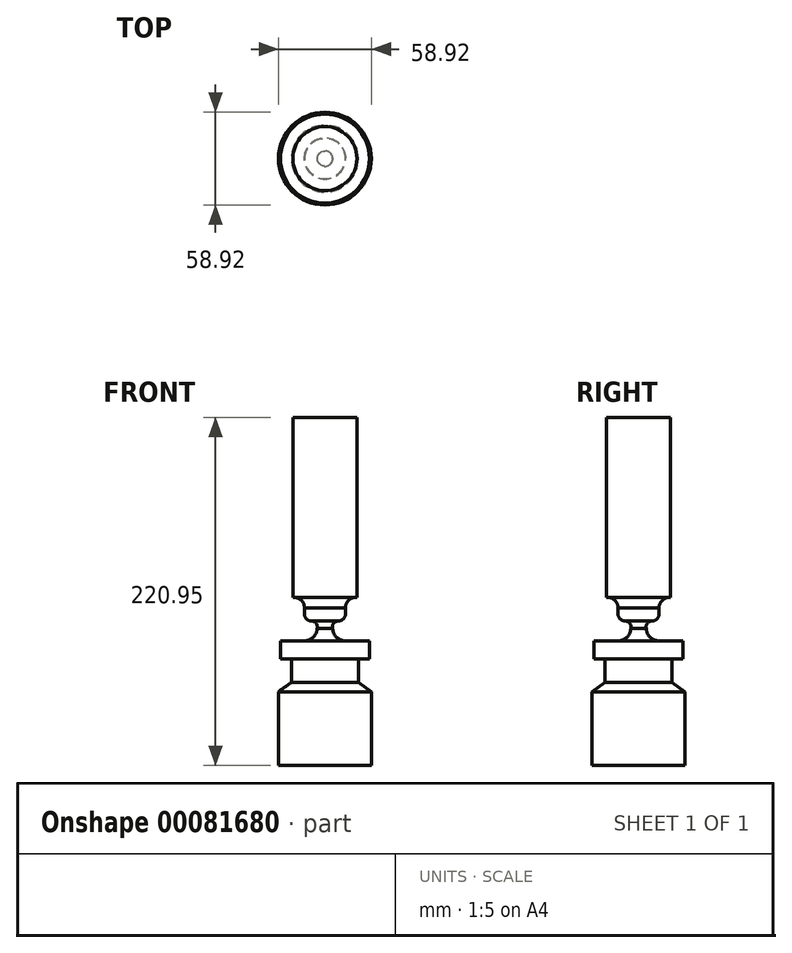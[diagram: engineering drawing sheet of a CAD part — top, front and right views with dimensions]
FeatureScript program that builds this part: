
annotation { "Feature Type Name" : "Feature", "Feature Type Description" : "" }
export const myFeature = defineFeature(function(context is Context, id is Id, definition is map)
    precondition{}
    {
        {
            var Q0;
            Q0=qCreatedBy(makeId("Front.planeOp"),FACE);
            var sketch = newSketch(context, id + "F0", { "sketchPlane" : qUnion([Q0])});
            skLineSegment(sketch, "E0", {"start": v(0, 0) * mm, "end": v(0, 45.72) * mm});
            skLineSegment(sketch, "E1", {"start": v(0, 0) * mm, "end": v(0, -45.72) * mm});
            skLineSegment(sketch, "E2", {"start": v(0, 45.72) * mm, "end": v(-20.32, 45.72) * mm});
            skLineSegment(sketch, "E3", {"start": v(-20.32, 45.72) * mm, "end": v(-20.32, 35.56) * mm});
            skArc(sketch, "E4", {"start": v(-20.32, 35.56) * mm, "mid": v(-15.12, 33.8) * mm, "end": v(-13.04, 28.73) * mm});
            skLineSegment(sketch, "E5", {"start": v(-13.04, 28.73) * mm, "end": v(-13.04, 25.17) * mm});
            skArc(sketch, "E6", {"start": v(-13.04, 25.17) * mm, "mid": v(-11.68, 21.89) * mm, "end": v(-8.4, 20.53) * mm});
            skArc(sketch, "E7", {"start": v(-8.4, 20.53) * mm, "mid": v(-5.55, 19.12) * mm, "end": v(-4.95, 16) * mm});
            skArc(sketch, "E8", {"start": v(-4.95, 16) * mm, "mid": v(-7.3, 10.3) * mm, "end": v(-13, 7.94) * mm});
            skLineSegment(sketch, "E9", {"start": v(-13, 7.94) * mm, "end": v(-28.24, 7.94) * mm});
            skLineSegment(sketch, "E10", {"start": v(-28.24, 7.94) * mm, "end": v(-28.24, -3.46) * mm});
            skLineSegment(sketch, "E11", {"start": v(-28.24, -3.46) * mm, "end": v(-21.23, -3.46) * mm});
            skLineSegment(sketch, "E12", {"start": v(-21.23, -3.46) * mm, "end": v(-21.23, -18.4) * mm});
            skLineSegment(sketch, "E13", {"start": v(-21.23, -18.4) * mm, "end": v(-29.46, -24.32) * mm});
            skLineSegment(sketch, "E14", {"start": v(-29.46, -24.32) * mm, "end": v(-29.46, -45.72) * mm});
            skLineSegment(sketch, "E15", {"start": v(-29.46, -45.72) * mm, "end": v(0, -45.72) * mm});
            skSolve(sketch);
        }
        {
            var Q0;
            Q0=makeQuery(id+"F0.imprint","IMPRINT",FACE,{"disambiguationData":[TD([[makeQuery(id+"F0.imprint","IMPRINT",EDGE,{"derivedFrom":sQuery(id+"F0.wireOp",EDGE,"E0")}),1.0]])]});
            var Q1;
            Q1=sQuery(id+"F0.wireOp",EDGE,"E0");
            revolve(context, id + "F1", {"entities" : qUnion([Q0]), "axis" : qUnion([Q1]), "revolveType" : RevolveType.FULL});
        }
        {
            var Q0;
            Q0=makeQuery(id+"F1.opRevolve","SWEPT_FACE",FACE,{"disambiguationData":[OSD([sQuery(id+"F0.wireOp",EDGE,"E2")])]});
            extrude(context, id + "F2", {"entities" : qUnion([Q0]), "operationType" : NewBodyOperationType.ADD, "depth" : 104.11 * mm});
        }
        {
            var Q0;
            Q0=makeQuery(id+"F1.opRevolve","SWEPT_FACE",FACE,{"disambiguationData":[OSD([sQuery(id+"F0.wireOp",EDGE,"E15")])]});
            extrude(context, id + "F3", {"entities" : qUnion([Q0]), "operationType" : NewBodyOperationType.ADD, "depth" : 25.4 * mm});
        }
    });
